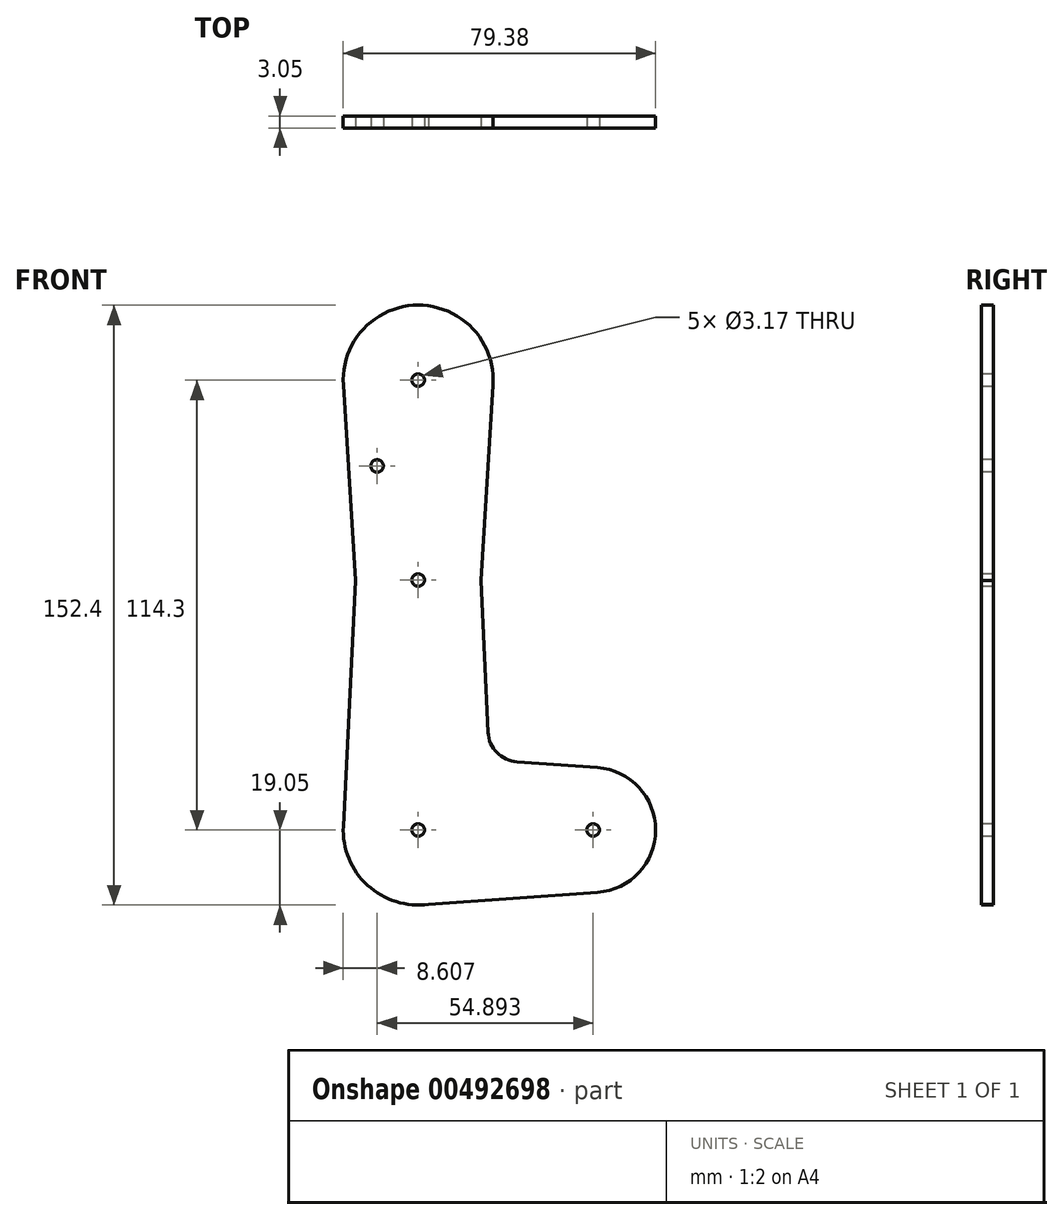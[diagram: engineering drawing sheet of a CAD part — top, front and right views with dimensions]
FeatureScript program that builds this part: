
annotation { "Feature Type Name" : "Feature", "Feature Type Description" : "" }
export const myFeature = defineFeature(function(context is Context, id is Id, definition is map)
    precondition{}
    {
        {
            var Q0;
            Q0=qCreatedBy(makeId("Front.planeOp"),FACE);
            var sketch = newSketch(context, id + "F0", { "sketchPlane" : qUnion([Q0])});
            skLineSegment(sketch, "E0", {"start": v(0, 0) * mm, "end": v(44.45, 0) * mm});
            skLineSegment(sketch, "E1", {"start": v(44.45, 0) * mm, "end": v(0, 0) * mm, "construction": true});
            skLineSegment(sketch, "E2", {"start": v(0, 114.3) * mm, "end": v(0, 0) * mm, "construction": true});
            skCircle(sketch, "E3", {"center": v(0, 0) * mm, "radius": 19.05 * mm});
            skCircle(sketch, "E4", {"center": v(0, 114.3) * mm, "radius": 19.05 * mm});
            skCircle(sketch, "E5", {"center": v(44.45, 0) * mm, "radius": 15.88 * mm});
            skCircle(sketch, "E6", {"center": v(0, 63.5) * mm, "radius": 15.88 * mm, "construction": true});
            skLineSegment(sketch, "E7", {"start": v(-19.01, 113.1) * mm, "end": v(-15.84, 62.5) * mm});
            skLineSegment(sketch, "E8", {"start": v(19.01, 113.1) * mm, "end": v(15.84, 62.5) * mm});
            skLineSegment(sketch, "E9", {"start": v(-15.86, 64.3) * mm, "end": v(-19.07, 0) * mm});
            skPoint(sketch, "E10.startSnap0", {"position": v(22.23, 0) * mm});
            skLineSegment(sketch, "E11", {"start": v(17.76, 24.85) * mm, "end": v(15.86, 64.27) * mm});
            skPoint(sketch, "E12.startSnap0", {"position": v(17.34, 33.62) * mm});
            skLineSegment(sketch, "E13", {"start": v(25.13, 17.3) * mm, "end": v(45.58, 15.83) * mm});
            skLineSegment(sketch, "E14", {"start": v(0, -19.05) * mm, "end": v(45.57, -15.84) * mm});
            skCircle(sketch, "E15", {"center": v(0, 0) * mm, "radius": 1.59 * mm});
            skCircle(sketch, "E16", {"center": v(44.45, 0) * mm, "radius": 1.59 * mm});
            skCircle(sketch, "E17", {"center": v(0, 63.5) * mm, "radius": 1.59 * mm});
            skCircle(sketch, "E18", {"center": v(0, 114.3) * mm, "radius": 1.59 * mm});
            skPoint(sketch, "E19.newPointB", {"position": v(18.82, 2.98) * mm});
            skArc(sketch, "E19.filletArc", {"start": v(17.76, 24.85) * mm, "mid": v(20.01, 19.67) * mm, "end": v(25.13, 17.3) * mm});
            skCircle(sketch, "E20", {"center": v(-10.44, 92.5) * mm, "radius": 1.59 * mm});
            skSolve(sketch);
        }
        {
            var Q0;
            Q0 = qSketchRegion(id + "F0", true);
            extrude(context, id + "F1", {"entities" : qUnion([Q0]), "oppositeDirection" : true, "depth" : 3.05 * mm});
        }
    });
